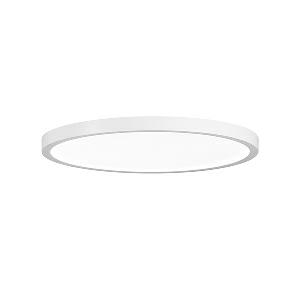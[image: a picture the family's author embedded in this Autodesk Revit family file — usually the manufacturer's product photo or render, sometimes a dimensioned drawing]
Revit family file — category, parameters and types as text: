
# Revit family: vivaa_fit_-_via_6000_930_d_00813053_abb9
name_source: partatom
category: Lighting Fixtures
units: mm (PartAtom-declared; Revit-internal decimal feet)

## family parameters
Cut with Voids When Loaded = No
Host = Face
Light Source = No
Part Type = Normal
Room Calculation Point = No
Round Connector Dimension = Use Diameter
Shared = No

## types (1)
- VIVAA.fit - VIA 6000/930/D (1 x LED, 6400 lm, 3000K)
    Apparent Load = 53 VA
    Approval mark = CE
    CIE Flux Codes = 66 90 98 45 100
    Color Rendering = 90-100
    Color Temperature = 3000K
    Control Gear = Electronic ballast
    Default Elevation = 1800 mm
    Description = VIA 6000/930/D|Surface-mounted luminaire.|light source:   Warm white   |work equipment: Power supply unit|luminous flux: 6400 lm|light distribution: Direct/indirect|class of protection: I|mains lead: Direct power supply 5 pin|glare control: optical film|special features: DALI Load 2x, Suitable as emergency lighting, Separated, direct and indirect light individually adjustable|
    Frequency = 50 Hz, 60 Hz
    Height = 48 mm  [stored 0.15748 ft]
    Lamp = 1 x LED
    Lamp Light Flux = 6400 lm
    Lamp count = 1
    Length = 450 mm
    Luminous efficacy = 121 lm/W
    Manufacturer = Waldmann
    ModVariant = No
    Model = 00813053
    Mounting Place = Ceiling
    Mounting Type = Surface mounted
    Number of Poles = 1
    OnlyDefault = Yes
    Power Factor = 1
    Product Name = VIVAA.fit - VIA 6000/930/D
    Product group = Ceiling mounted luminaire
    ProductGroupID = 3
    Protection Class = Protection class I
    Protection Degree = Degree of protection
    RLX_Detail_Level = 1
    RLX_Emergency_Light_Flux = 0 lm
    RLX_Emergency_Type = 0
    RLX_Emergency_Type_DB = No
    RlxData = <blob elided: 20537 chars, md5=a109ee1c>
    Socket = socket
    Standby Power = 0 W
    System Light Flux = 6400 lm
    System Power = 53 W
    Type Comments = Product without accessories
    Type Image = vivaa_2.0_anbau_450mm.jpg
    URL = http://relux.com
    VarID = ---
    Voltage = 230 V
    Voltage Range = 220-240 V
    Weight = 0.00 kg
    Width = 0 mm  [stored 0 ft]

note: [stored X ft] marks values corroborated as IEEE doubles in the binary element streams (Revit-internal decimal feet)

## geometry (parser evidence)
native form markers: Blend x4, Sweep x13
no freeform markers — native parametric forms only
